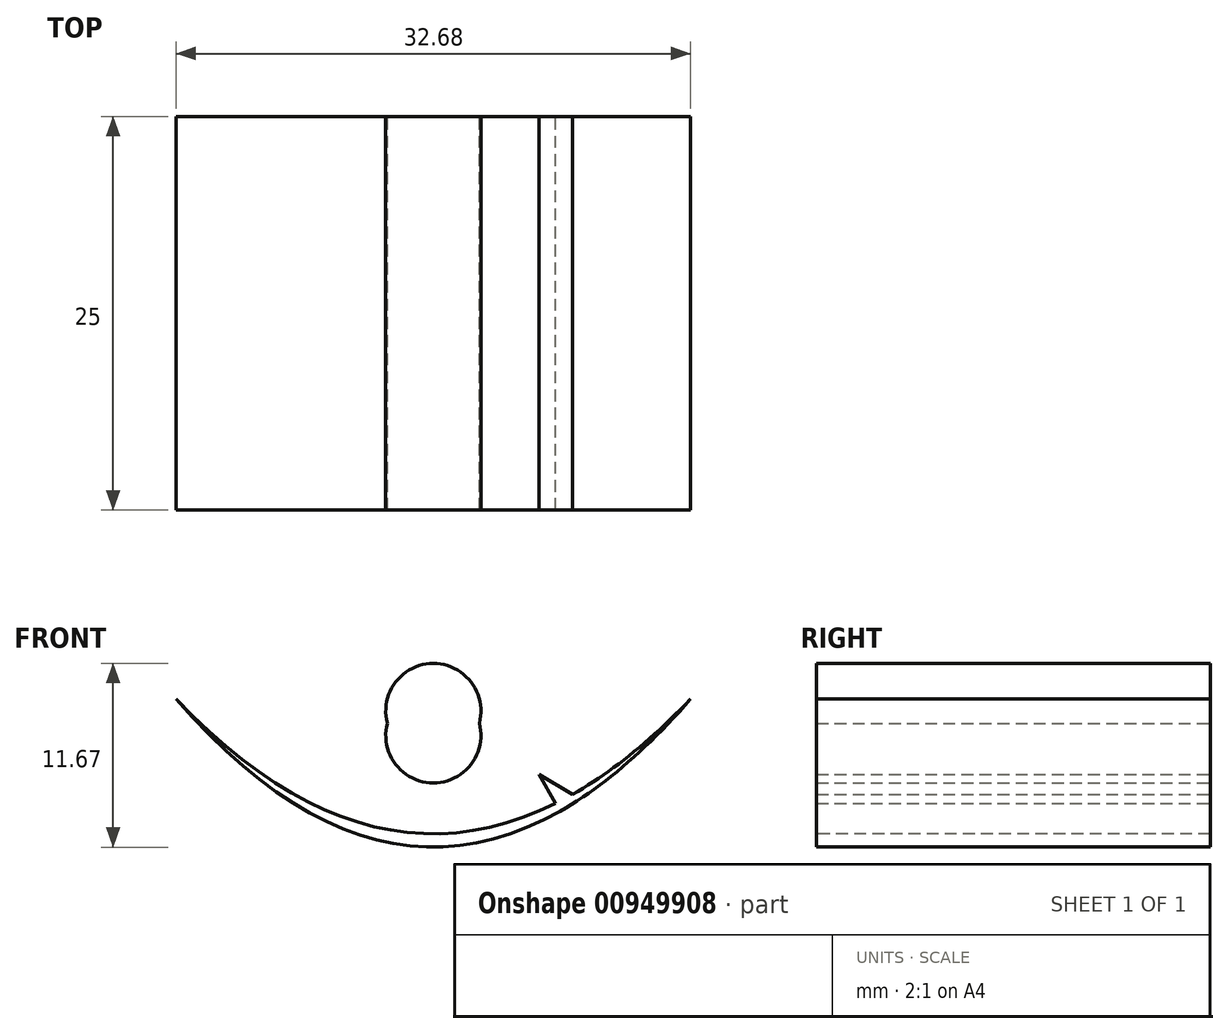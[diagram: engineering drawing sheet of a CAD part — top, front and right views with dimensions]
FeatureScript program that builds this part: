
annotation { "Feature Type Name" : "Feature", "Feature Type Description" : "" }
export const myFeature = defineFeature(function(context is Context, id is Id, definition is map)
    precondition{}
    {
        {
            var Q0;
            Q0=qCreatedBy(makeId("Front.planeOp"),FACE);
            var sketch = newSketch(context, id + "F0", { "sketchPlane" : qUnion([Q0])});
            skLineSegment(sketch, "E0", {"start": v(0, 0) * mm, "end": v(32.68, 0) * mm, "construction": true});
            skLineSegment(sketch, "E1", {"start": v(32.68, 0) * mm, "end": v(16.34, -17.12) * mm, "construction": true});
            skPoint(sketch, "E1.endSnap0", {"position": v(16.34, 0) * mm});
            skLineSegment(sketch, "E2", {"start": v(16.34, -17.12) * mm, "end": v(10.9, -11.41) * mm, "construction": true});
            skLineSegment(sketch, "E3", {"start": v(10.9, -11.41) * mm, "end": v(5.45, -5.7) * mm, "construction": true});
            skLineSegment(sketch, "E4", {"start": v(5.45, -5.7) * mm, "end": v(0, 0) * mm, "construction": true});
            skFitSpline(sketch, "E5", {"points": [v(0, 0) * mm, v(32.68, 0) * mm], "startDerivative": vector(32.68, -34.24) * mm, "endDerivative": vector(32.68, 34.24) * mm});
            skLineSegment(sketch, "E6", {"start": v(25.19, 0.13) * mm, "end": v(25.19, -6.05) * mm});
            skLineSegment(sketch, "E7", {"start": v(25.19, -6.05) * mm, "end": v(19.65, 3.7) * mm});
            skLineSegment(sketch, "E8.MirrorCS", {"start": v(19.88, -2.88) * mm, "end": v(25.19, -6.05) * mm});
            skCircle(sketch, "E9", {"center": v(16.34, -0.76) * mm, "radius": 3.02 * mm});
            skLineSegment(sketch, "E10", {"start": v(32.68, 0) * mm, "end": v(16.34, -18.81) * mm, "construction": true});
            skLineSegment(sketch, "E11", {"start": v(16.34, -18.81) * mm, "end": v(10.9, -12.54) * mm, "construction": true});
            skLineSegment(sketch, "E12", {"start": v(10.9, -12.54) * mm, "end": v(5.45, -6.27) * mm, "construction": true});
            skLineSegment(sketch, "E13", {"start": v(5.45, -6.27) * mm, "end": v(0, 0) * mm, "construction": true});
            skFitSpline(sketch, "E14", {"points": [v(0, 0) * mm, v(32.68, 0) * mm], "startDerivative": vector(32.68, -37.63) * mm, "endDerivative": vector(32.68, 37.63) * mm});
            skLineSegment(sketch, "E15", {"start": v(24.4, -7.12) * mm, "end": v(24.4, -16.31) * mm});
            skLineSegment(sketch, "E16", {"start": v(24.4, -7.12) * mm, "end": v(20.5, -0.26) * mm});
            skLineSegment(sketch, "E17.MirrorCS", {"start": v(24.4, -7.12) * mm, "end": v(32.28, -11.84) * mm});
            skCircle(sketch, "E18", {"center": v(16.34, -2.3) * mm, "radius": 3.02 * mm});
            skSolve(sketch);
        }
        {
            var Q0;
            Q0 = qSketchRegion(id + "F0", true);
            extrude(context, id + "F1", {"entities" : qUnion([Q0]), "depth" : 25 * mm, "offsetDistance" : 25 * mm});
        }
    });
